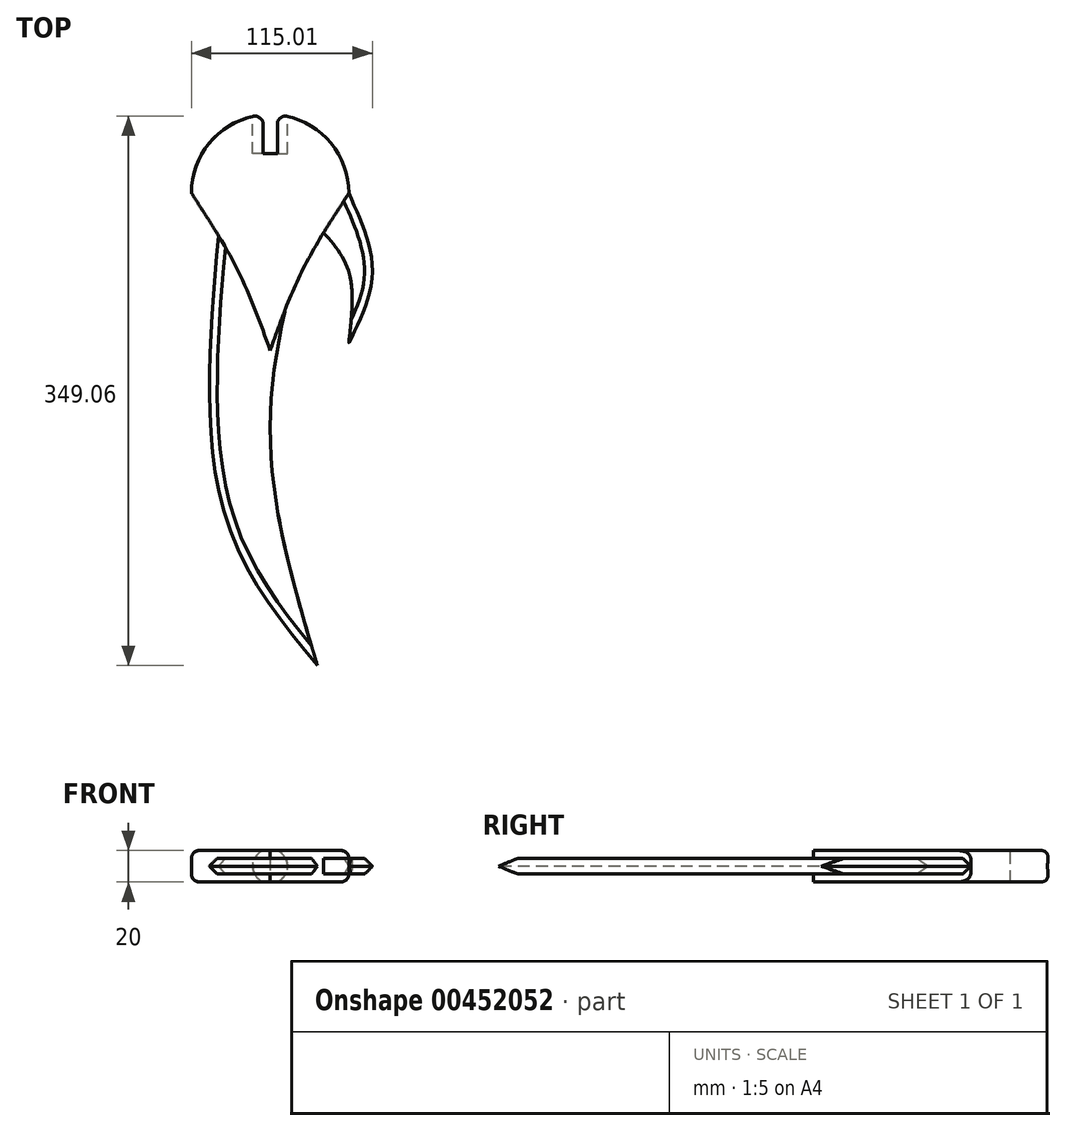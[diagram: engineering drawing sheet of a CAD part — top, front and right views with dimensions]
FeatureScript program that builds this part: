
annotation { "Feature Type Name" : "Feature", "Feature Type Description" : "" }
export const myFeature = defineFeature(function(context is Context, id is Id, definition is map)
    precondition{}
    {
        {
            var Q0;
            Q0=qCreatedBy(makeId("Top.planeOp"),FACE);
            var sketch = newSketch(context, id + "F0", { "sketchPlane" : qUnion([Q0])});
            skArc(sketch, "E0", {"start": v(50, -0.04) * mm, "mid": v(0.02, 50) * mm, "end": v(-50, 0) * mm});
            skFitSpline(sketch, "E1", {"points": [v(-50, 0) * mm, v(-20, -50) * mm, v(0, -100) * mm], "startDerivative": vector(63.42, -97.04) * mm, "endDerivative": vector(36.4, -103) * mm});
            skFitSpline(sketch, "E2", {"points": [v(50, -0.04) * mm, v(20, -50) * mm, v(0, -100) * mm], "startDerivative": vector(-63.42, -97.04) * mm, "endDerivative": vector(-36.4, -103) * mm});
            skFitSpline(sketch, "E3", {"points": [v(-30, 0) * mm, v(-30, -200) * mm, v(30, -300) * mm], "startDerivative": vector(-39.29, -387.24) * mm, "endDerivative": vector(168.57, -204.6) * mm});
            skFitSpline(sketch, "E4", {"points": [v(30, -300) * mm, v(0, -150) * mm, v(30, 0) * mm], "startDerivative": vector(-90, 300) * mm, "endDerivative": vector(90, 300) * mm});
            skLineSegment(sketch, "E5", {"start": v(9.12, -75) * mm, "end": v(9.38, -75) * mm});
            skFitSpline(sketch, "E6", {"points": [v(34.01, -25) * mm, v(50, -50) * mm, v(50, -95) * mm], "startDerivative": vector(43.7, -50.01) * mm, "endDerivative": vector(-9.85, -88.65) * mm});
            skFitSpline(sketch, "E7", {"points": [v(50, -0.04) * mm, v(65, -50) * mm, v(50, -95) * mm], "startDerivative": vector(44.67, -99.06) * mm, "endDerivative": vector(-45.39, -90.88) * mm});
            skPoint(sketch, "E8.start.orphan", {"position": v(0.02, 50) * mm});
            skLineSegment(sketch, "E9.bottom", {"start": v(0, 60) * mm, "end": v(11.02, 60) * mm});
            skLineSegment(sketch, "E9.top", {"start": v(0, 40) * mm, "end": v(11.02, 40) * mm});
            skLineSegment(sketch, "E9.right", {"start": v(11.02, 60) * mm, "end": v(11.02, 40) * mm});
            skLineSegment(sketch, "E10", {"start": v(0.02, 50) * mm, "end": v(0, 60) * mm});
            skLineSegment(sketch, "E11", {"start": v(0.02, 50) * mm, "end": v(0, 40) * mm});
            skSolve(sketch);
        }
        {
            var Q0;
            {var subQ5=sQuery(id+"F0.wireOp",EDGE,"E9.top");Q0=makeQuery(id+"F0.imprint","IMPRINT",FACE,{"disambiguationData":[TD([[makeQuery(id+"F0.imprint","IMPRINT",EDGE,{"derivedFrom":subQ5}),-1.0]])]});}
            var Q1;
            {var subQ5=sQuery(id+"F0.wireOp",EDGE,"E9.top");Q1=makeQuery(id+"F0.imprint","IMPRINT",FACE,{"disambiguationData":[TD([[makeQuery(id+"F0.imprint","IMPRINT",EDGE,{"derivedFrom":subQ5}),1.0]])]});}
            extrude(context, id + "F1", {"entities" : qUnion([Q0, Q1]), "depth" : 10 * mm, "hasSecondDirection" : true, "secondDirectionOppositeDirection" : true, "secondDirectionDepth" : 10 * mm});
        }
        {
            var Q0;
            {var subQ1=sQuery(id+"F0.wireOp",EDGE,"E3");Q0=makeQuery(id+"F0.imprint","IMPRINT",FACE,{"disambiguationData":[TD([[makeQuery(id+"F0.imprint","IMPRINT",EDGE,{"derivedFrom":subQ1}),1.0]])]});}
            var Q1;
            {var subQ2=sQuery(id+"F0.wireOp",EDGE,"E6");Q1=makeQuery(id+"F0.imprint","IMPRINT",FACE,{"disambiguationData":[TD([[makeQuery(id+"F0.imprint","IMPRINT",EDGE,{"derivedFrom":subQ2}),1.0]])]});}
            extrude(context, id + "F2", {"entities" : qUnion([Q0, Q1]), "operationType" : NewBodyOperationType.ADD, "depth" : 5 * mm, "hasSecondDirection" : true, "secondDirectionOppositeDirection" : true, "secondDirectionDepth" : 5 * mm});
        }
        {
            var Q0;
            Q0=makeQuery(id+"F2.opExtrude","CAP_EDGE",EDGE,{"disambiguationData":[OSD([sQuery(id+"F0.wireOp",EDGE,"E3")])],"isStart":false});
            chamfer(context, id + "F3", {"entities" : qUnion([Q0]), "width" : 5 * mm, "tangentPropagation" : true});
        }
        {
            var Q0;
            Q0=makeQuery(id+"F2.opExtrude","CAP_EDGE",EDGE,{"disambiguationData":[OSD([sQuery(id+"F0.wireOp",EDGE,"E3")])],"isStart":true});
            chamfer(context, id + "F4", {"entities" : qUnion([Q0]), "width" : 5 * mm, "tangentPropagation" : true});
        }
        {
            var Q0;
            Q0=makeQuery(id+"F2.opExtrude","CAP_EDGE",EDGE,{"disambiguationData":[OSD([sQuery(id+"F0.wireOp",EDGE,"E7")])],"isStart":false});
            var Q1;
            Q1=makeQuery(id+"F2.opExtrude","CAP_EDGE",EDGE,{"disambiguationData":[OSD([sQuery(id+"F0.wireOp",EDGE,"E7")])],"isStart":true});
            chamfer(context, id + "F5", {"entities" : qUnion([Q0, Q1]), "width" : 5 * mm, "tangentPropagation" : true});
        }
        {
            var Q0;
            Q0=makeQuery(id+"F1.opExtrude","CAP_EDGE",EDGE,{"disambiguationData":[OSD([sQuery(id+"F0.wireOp",EDGE,"E0")])],"isStart":false});
            fillet(context, id + "F6", {"entities" : qUnion([Q0]), "radius" : 5 * mm, "tangentPropagation" : true, "allowEdgeOverflow" : false});
        }
        {
            var Q0;
            Q0=makeQuery(id+"F1.opExtrude","CAP_EDGE",EDGE,{"disambiguationData":[OSD([sQuery(id+"F0.wireOp",EDGE,"E0")])],"isStart":true});
            fillet(context, id + "F7", {"entities" : qUnion([Q0]), "radius" : 5 * mm, "tangentPropagation" : true, "allowEdgeOverflow" : false});
        }
        {
            var Q0;
            Q0=qCreatedBy(makeId("Front.planeOp"),FACE);
            cPlane(context, id + "F8", {"entities" : qUnion([Q0]), "cplaneType" : CPlaneType.OFFSET, "offset" : 50 * mm, "oppositeDirection" : true, "width" : 150 * mm, "height" : 150 * mm});
        }
        {
            var Q0;
            Q0=qCreatedBy(id+"F8.planeOp",FACE);
            var sketch = newSketch(context, id + "F9", { "sketchPlane" : qUnion([Q0])});
            skCircle(sketch, "E12", {"center": v(0, 0) * mm, "radius": 11 * mm});
            skSolve(sketch);
        }
        {
            var Q0;
            Q0=makeQuery(id+"F9.imprint","IMPRINT",FACE,{"disambiguationData":[TD([[makeQuery(id+"F9.imprint","IMPRINT",EDGE,{"derivedFrom":sQuery(id+"F9.wireOp",EDGE,"E12")}),1.0]])]});
            extrude(context, id + "F10", {"entities" : qUnion([Q0]), "operationType" : NewBodyOperationType.REMOVE, "depth" : 25 * mm});
        }
    });
